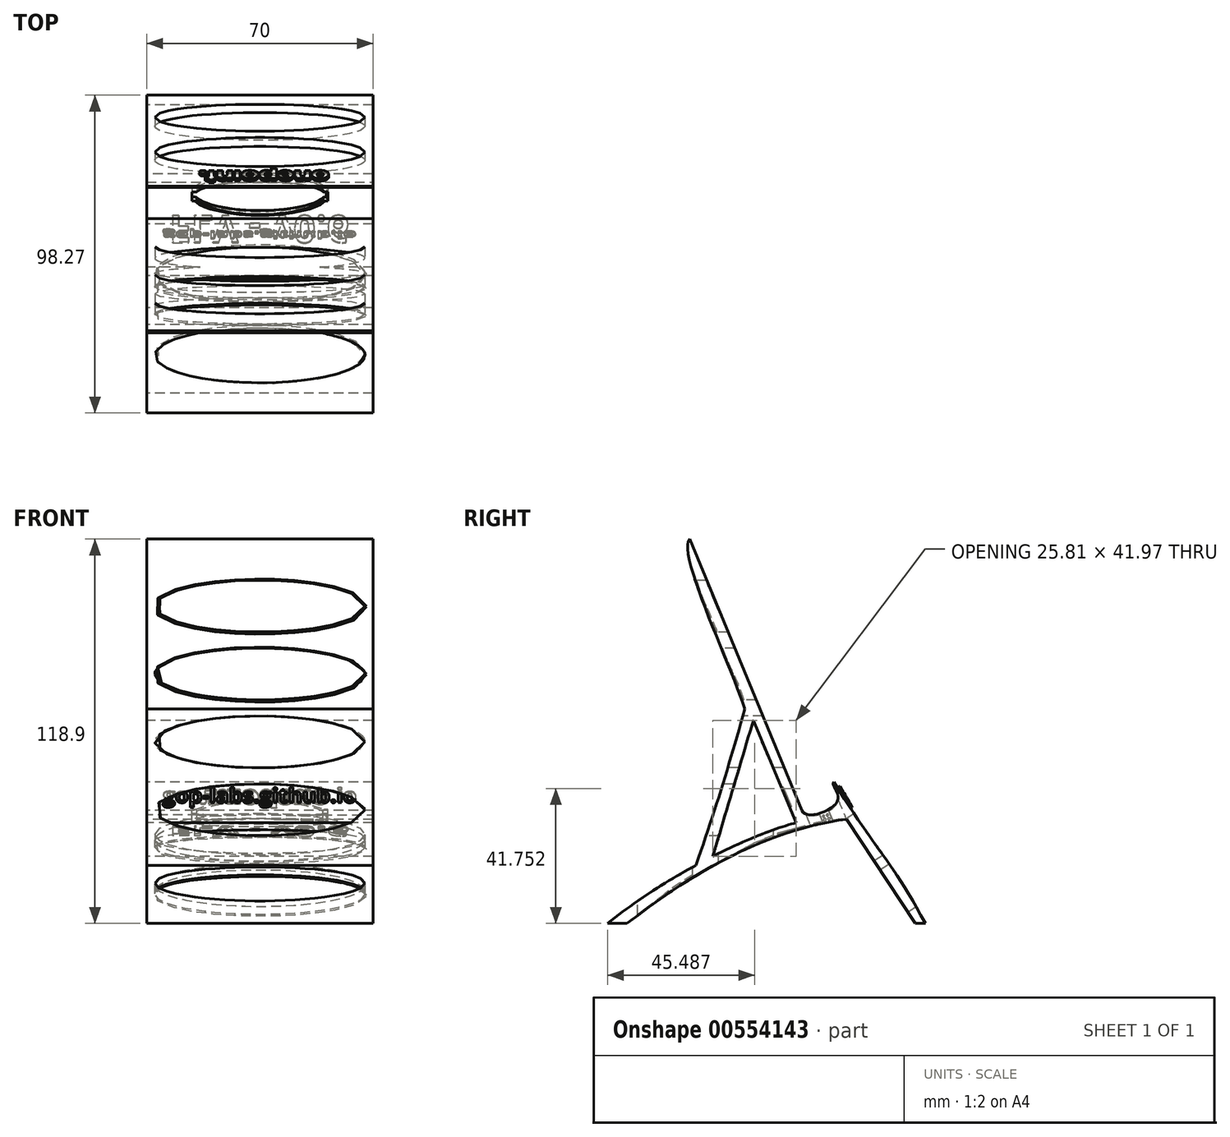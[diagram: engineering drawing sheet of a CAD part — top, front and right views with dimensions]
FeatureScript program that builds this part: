
annotation { "Feature Type Name" : "Feature", "Feature Type Description" : "" }
export const myFeature = defineFeature(function(context is Context, id is Id, definition is map)
    precondition{}
    {
        {
            var Q0;
            Q0=qCreatedBy(makeId("Right.planeOp"),FACE);
            var sketch = newSketch(context, id + "F0", { "sketchPlane" : qUnion([Q0])});
            skFitSpline(sketch, "E0", {"points": [v(42.97, 20.37) * mm, v(14.77, 64.07) * mm], "startDerivative": vector(-33.57, 62.35) * mm, "endDerivative": vector(-38.78, 64) * mm});
            skLineSegment(sketch, "E1", {"start": v(-29.92, 139.27) * mm, "end": v(4.83, 55.39) * mm});
            skFitSpline(sketch, "E2", {"points": [v(4.83, 55.39) * mm, v(15.94, 58.63) * mm, v(14.77, 64.07) * mm], "startDerivative": vector(5.7, -17.02) * mm, "endDerivative": vector(10.42, 3.26) * mm});
            skLineSegment(sketch, "E3", {"start": v(18.6, 52.58) * mm, "end": v(39.9, 20.37) * mm});
            skLineSegment(sketch, "E4", {"start": v(-10.23, 83.1) * mm, "end": v(3.1, 51.52) * mm});
            skFitSpline(sketch, "E5", {"points": [v(-29.92, 139.27) * mm, v(-12.82, 86.66) * mm], "startDerivative": vector(-12.17, -12.55) * mm, "endDerivative": vector(13.11, -40.92) * mm});
            skFitSpline(sketch, "E6", {"points": [v(3.1, 51.52) * mm, v(-55.3, 20.37) * mm], "startDerivative": vector(-34.97, -8.7) * mm, "endDerivative": vector(-63.71, -51.04) * mm});
            skFitSpline(sketch, "E7", {"points": [v(18.6, 52.58) * mm, v(-49.24, 20.37) * mm], "startDerivative": vector(-55.78, -6.95) * mm, "endDerivative": vector(-79.56, -62.3) * mm});
            skLineSegment(sketch, "E8", {"start": v(-49.24, 20.37) * mm, "end": v(-55.3, 20.37) * mm});
            skLineSegment(sketch, "E9", {"start": v(42.97, 20.37) * mm, "end": v(39.9, 20.37) * mm});
            skLineSegment(sketch, "E10", {"start": v(39.9, 20.37) * mm, "end": v(-49.24, 20.37) * mm});
            skFitSpline(sketch, "E11", {"points": [v(-10.23, 83.1) * mm, v(-22.72, 41.14) * mm], "startDerivative": vector(-11.4, -38.7) * mm, "endDerivative": vector(-11.4, -38.7) * mm});
            skFitSpline(sketch, "E12", {"points": [v(-12.82, 86.66) * mm, v(-27.98, 38.37) * mm], "startDerivative": vector(-14.28, -50.37) * mm, "endDerivative": vector(-17.92, -50.53) * mm});
            skSolve(sketch);
        }
        {
            var Q0;
            Q0=makeQuery(id+"F0.imprint","IMPRINT",FACE,{"disambiguationData":[TD([[makeQuery(id+"F0.imprint","IMPRINT",EDGE,{"derivedFrom":sQuery(id+"F0.wireOp",EDGE,"e2dd9e04-bce8-43ee-a2f2-a46b7d135692")}),-1.0]])]});
            var Q1;
            Q1=makeQuery(id+"F0.imprint","IMPRINT",FACE,{"disambiguationData":[TD([[makeQuery(id+"F0.imprint","IMPRINT",EDGE,{"derivedFrom":sQuery(id+"F0.wireOp",EDGE,"dd02e322-1caa-4adf-9807-8f987be65d11")}),1.0]])]});
            var Q2;
            Q2=makeQuery(id+"F0.imprint","IMPRINT",FACE,{"disambiguationData":[TD([[makeQuery(id+"F0.imprint","IMPRINT",EDGE,{"derivedFrom":sQuery(id+"F0.wireOp",EDGE,"E0")}),1.0]])]});
            var Q3;
            {var subQ0=sQuery(id+"F0.wireOp",EDGE,"E6");Q3=makeQuery(id+"F0.imprint","IMPRINT",FACE,{"disambiguationData":[TD([[makeQuery(id+"F0.imprint","IMPRINT",EDGE,{"derivedFrom":subQ0}),1.0]])]});}
            extrude(context, id + "F1", {"entities" : qUnion([Q0, Q1, Q2, Q3]), "depth" : 70 * mm});
        }
        {
            var Q0;
            Q0=makeQuery(id+"F1.opExtrude","SWEPT_FACE",FACE,{"disambiguationData":[OSD([sQuery(id+"F0.wireOp",EDGE,"E3")])]});
            var sketch = newSketch(context, id + "F2", { "sketchPlane" : qUnion([Q0])});
            skEllipse(sketch, "E13", {"center": v(35, 25.97) * mm, "majorRadius": 32.5 * mm, "minorRadius": 7.82 * mm, "majorAxis": v(1, 0)});
            skEllipse(sketch, "E14.0.1.0", {"center": v(35, 6.97) * mm, "majorRadius": 32.5 * mm, "minorRadius": 7.82 * mm, "majorAxis": v(1, 0)});
            skLineSegment(sketch, "E14.direction1", {"start": v(35, 25.97) * mm, "end": v(57.03, 25.97) * mm, "construction": true});
            skLineSegment(sketch, "E14.direction2", {"start": v(35, 25.97) * mm, "end": v(35, 6.97) * mm, "construction": true});
            skSolve(sketch);
        }
        {
            var Q0;
            Q0=qSketchRegion(id+"F2",true);
            var Q1;
            Q1=makeQuery(id+"F1.opExtrude","SWEPT_FACE",FACE,{"disambiguationData":[OSD([sQuery(id+"F0.wireOp",EDGE,"E0")])]});
            extrude(context, id + "F3", {"entities" : qUnion([Q0]), "operationType" : NewBodyOperationType.REMOVE, "endBound" : BoundingType.UP_TO_SURFACE, "oppositeDirection" : true, "endBoundEntityFace" : qUnion([Q1]), "depth" : 25 * mm});
        }
        {
            var Q0;
            Q0=qCreatedBy(makeId("Top.planeOp"),FACE);
            var sketch = newSketch(context, id + "F4", { "sketchPlane" : qUnion([Q0])});
            skEllipse(sketch, "E15", {"center": v(35, -37.48) * mm, "majorRadius": 32.5 * mm, "minorRadius": 8.5 * mm, "majorAxis": v(1, 0)});
            skEllipse(sketch, "E16.0.1.0", {"center": v(35, -12.48) * mm, "majorRadius": 32.5 * mm, "minorRadius": 8.5 * mm, "majorAxis": v(1, 0)});
            skLineSegment(sketch, "E16.direction1", {"start": v(35, -37.48) * mm, "end": v(60, -37.48) * mm, "construction": true});
            skLineSegment(sketch, "E16.direction2", {"start": v(35, -37.48) * mm, "end": v(35, -12.48) * mm, "construction": true});
            skSolve(sketch);
        }
        {
            var Q0;
            Q0=makeQuery(id+"F4.imprint","IMPRINT",FACE,{"disambiguationData":[TD([[makeQuery(id+"F4.imprint","IMPRINT",EDGE,{"derivedFrom":sQuery(id+"F4.wireOp",EDGE,"E16.0.1.0")}),1.0]])]});
            var Q1;
            Q1=makeQuery(id+"F4.imprint","IMPRINT",FACE,{"disambiguationData":[TD([[makeQuery(id+"F4.imprint","IMPRINT",EDGE,{"derivedFrom":sQuery(id+"F4.wireOp",EDGE,"E16.0.2.0")}),1.0]])]});
            var Q2;
            Q2=makeQuery(id+"F1.opExtrude","SWEPT_FACE",FACE,{"disambiguationData":[OSD([sQuery(id+"F0.wireOp",EDGE,"E6")])]});
            extrude(context, id + "F5", {"entities" : qUnion([Q0, Q1]), "operationType" : NewBodyOperationType.REMOVE, "endBound" : BoundingType.UP_TO_SURFACE, "endBoundEntityFace" : qUnion([Q2]), "depth" : 25 * mm});
        }
        {
            var Q0;
            Q0=qCreatedBy(makeId("Front.planeOp"),FACE);
            cPlane(context, id + "F6", {"entities" : qUnion([Q0]), "cplaneType" : CPlaneType.OFFSET, "offset" : 70 * mm, "width" : 150 * mm, "height" : 150 * mm});
        }
        {
            var Q0;
            Q0=qCreatedBy(id+"F6.planeOp",FACE);
            var sketch = newSketch(context, id + "F7", { "sketchPlane" : qUnion([Q0])});
            skEllipse(sketch, "E17", {"center": v(35, 118.52) * mm, "majorRadius": 32.5 * mm, "minorRadius": 8 * mm, "majorAxis": v(1, 0)});
            skEllipse(sketch, "E18.0.1.0", {"center": v(35, 97.52) * mm, "majorRadius": 32.5 * mm, "minorRadius": 8 * mm, "majorAxis": v(1, 0)});
            skEllipse(sketch, "E18.0.2.0", {"center": v(35, 76.52) * mm, "majorRadius": 32.5 * mm, "minorRadius": 8 * mm, "majorAxis": v(1, 0)});
            skEllipse(sketch, "E18.0.3.0", {"center": v(35, 55.52) * mm, "majorRadius": 32.5 * mm, "minorRadius": 8 * mm, "majorAxis": v(1, 0)});
            skEllipse(sketch, "E18.0.4.0", {"center": v(35, 34.52) * mm, "majorRadius": 32.5 * mm, "minorRadius": 8 * mm, "majorAxis": v(1, 0)});
            skEllipse(sketch, "E18.0.5.0", {"center": v(35, 13.52) * mm, "majorRadius": 32.5 * mm, "minorRadius": 8 * mm, "majorAxis": v(1, 0)});
            skLineSegment(sketch, "E18.direction1", {"start": v(35, 118.52) * mm, "end": v(60, 118.52) * mm, "construction": true});
            skLineSegment(sketch, "E18.direction2", {"start": v(35, 118.52) * mm, "end": v(35, 97.52) * mm, "construction": true});
            skSolve(sketch);
        }
        {
            var Q0;
            Q0=makeQuery(id+"F7.imprint","IMPRINT",FACE,{"disambiguationData":[TD([[makeQuery(id+"F7.imprint","IMPRINT",EDGE,{"derivedFrom":sQuery(id+"F7.wireOp",EDGE,"E18.0.3.0")}),1.0]])]});
            var Q1;
            Q1=makeQuery(id+"F1.opExtrude","SWEPT_FACE",FACE,{"disambiguationData":[OSD([sQuery(id+"F0.wireOp",EDGE,"E11")])]});
            extrude(context, id + "F8", {"entities" : qUnion([Q0]), "operationType" : NewBodyOperationType.REMOVE, "endBound" : BoundingType.UP_TO_SURFACE, "oppositeDirection" : true, "endBoundEntityFace" : qUnion([Q1]), "depth" : 25 * mm});
        }
        {
            var Q0;
            Q0=makeQuery(id+"F7.imprint","IMPRINT",FACE,{"disambiguationData":[TD([[makeQuery(id+"F7.imprint","IMPRINT",EDGE,{"derivedFrom":sQuery(id+"F7.wireOp",EDGE,"E17")}),1.0]])]});
            var Q1;
            Q1=makeQuery(id+"F7.imprint","IMPRINT",FACE,{"disambiguationData":[TD([[makeQuery(id+"F7.imprint","IMPRINT",EDGE,{"derivedFrom":sQuery(id+"F7.wireOp",EDGE,"E18.0.1.0")}),1.0]])]});
            var Q2;
            Q2=makeQuery(id+"F7.imprint","IMPRINT",FACE,{"disambiguationData":[TD([[makeQuery(id+"F7.imprint","IMPRINT",EDGE,{"derivedFrom":sQuery(id+"F7.wireOp",EDGE,"E18.0.2.0")}),1.0]])]});
            var Q3;
            Q3=makeQuery(id+"F1.opExtrude","SWEPT_FACE",FACE,{"disambiguationData":[OSD([sQuery(id+"F0.wireOp",EDGE,"E1")])]});
            extrude(context, id + "F9", {"entities" : qUnion([Q0, Q1, Q2]), "operationType" : NewBodyOperationType.REMOVE, "endBound" : BoundingType.UP_TO_SURFACE, "oppositeDirection" : true, "endBoundEntityFace" : qUnion([Q3]), "depth" : 25 * mm});
        }
        {
            var Q0;
            Q0=makeQuery(id+"F1.opExtrude","SWEPT_FACE",FACE,{"disambiguationData":[OSD([sQuery(id+"F0.wireOp",EDGE,"E1")])]});
            var Q1;
            Q1=makeQuery(id+"F1.opExtrude","SWEPT_EDGE",EDGE,{"disambiguationData":[OSD([sQuery(id+"F0.wireOp",EDGE,"E1"),sQuery(id+"F0.wireOp",EDGE,"E5")])]});
            cPlane(context, id + "F10", {"entities" : qUnion([Q0, Q1]), "cplaneType" : CPlaneType.LINE_ANGLE, "offset" : 25 * mm, "angle" : 90 * degree, "width" : 150 * mm, "height" : 150 * mm});
        }
        {
            var Q0;
            Q0=qCreatedBy(id+"F10.planeOp",FACE);
            var sketch = newSketch(context, id + "F11", { "sketchPlane" : qUnion([Q0])});
            skEllipse(sketch, "E19", {"center": v(35, 31.76) * mm, "majorRadius": 20.25 * mm, "minorRadius": 5.5 * mm, "majorAxis": v(-1, 0)});
            skLineSegment(sketch, "E20.bottom", {"start": v(14, 30.26) * mm, "end": v(56, 30.26) * mm});
            skLineSegment(sketch, "E20.top", {"start": v(14, 33.26) * mm, "end": v(56, 33.26) * mm});
            skLineSegment(sketch, "E20.left", {"start": v(14, 30.26) * mm, "end": v(14, 33.26) * mm});
            skLineSegment(sketch, "E20.right", {"start": v(56, 30.26) * mm, "end": v(56, 33.26) * mm});
            skSolve(sketch);
        }
        {
            var Q0;
            Q0=qSketchRegion(id+"F11",true);
            var Q1;
            Q1=makeQuery(id+"F1.opExtrude","SWEPT_FACE",FACE,{"disambiguationData":[OSD([sQuery(id+"F0.wireOp",EDGE,"E7")])]});
            extrude(context, id + "F12", {"entities" : qUnion([Q0]), "operationType" : NewBodyOperationType.REMOVE, "endBound" : BoundingType.THROUGH_ALL, "oppositeDirection" : true, "endBoundEntityFace" : qUnion([Q1]), "depth" : 25 * mm});
        }
        {
            var Q0;
            Q0=makeQuery(id+"F3.boolean.opBoolean","COPY",EDGE,{"derivedFrom":makeQuery(id+"F3.opExtrude","TWEAK_EDGE",EDGE,{"derivedFrom":[makeQuery(id+"F1.opExtrude","SWEPT_FACE",FACE,{"disambiguationData":[OSD([sQuery(id+"F0.wireOp",EDGE,"E0")])]}),makeQuery(id+"F2.imprint","IMPRINT",EDGE,{"derivedFrom":sQuery(id+"F2.wireOp",EDGE,"E13")})]})});
            var Q1;
            Q1=makeQuery(id+"F3.boolean.opBoolean","COPY",EDGE,{"derivedFrom":makeQuery(id+"F3.opExtrude","TWEAK_EDGE",EDGE,{"derivedFrom":[makeQuery(id+"F1.opExtrude","SWEPT_FACE",FACE,{"disambiguationData":[OSD([sQuery(id+"F0.wireOp",EDGE,"E0")])]}),makeQuery(id+"F2.imprint","IMPRINT",EDGE,{"derivedFrom":sQuery(id+"F2.wireOp",EDGE,"E14.0.1.0")})]})});
            var Q2;
            Q2=makeQuery(id+"F3.boolean.opBoolean","COPY",EDGE,{"derivedFrom":makeQuery(id+"F3.opExtrude","TWEAK_EDGE",EDGE,{"derivedFrom":[makeQuery(id+"F1.opExtrude","SWEPT_FACE",FACE,{"disambiguationData":[OSD([sQuery(id+"F0.wireOp",EDGE,"E0")])]}),makeQuery(id+"F2.imprint","IMPRINT",EDGE,{"derivedFrom":sQuery(id+"F2.wireOp",EDGE,"E14.0.2.0")})]})});
            var Q3;
            Q3=makeQuery(id+"F3.boolean.opBoolean","COPY",EDGE,{"derivedFrom":makeQuery(id+"F3.opExtrude","CAP_EDGE",EDGE,{"disambiguationData":[OSD([sQuery(id+"F2.wireOp",EDGE,"E13")])],"isStart":true})});
            var Q4;
            Q4=makeQuery(id+"F3.boolean.opBoolean","COPY",EDGE,{"derivedFrom":makeQuery(id+"F3.opExtrude","CAP_EDGE",EDGE,{"disambiguationData":[OSD([sQuery(id+"F2.wireOp",EDGE,"E14.0.1.0")])],"isStart":true})});
            var Q5;
            Q5=makeQuery(id+"F3.boolean.opBoolean","COPY",EDGE,{"derivedFrom":makeQuery(id+"F3.opExtrude","CAP_EDGE",EDGE,{"disambiguationData":[OSD([sQuery(id+"F2.wireOp",EDGE,"E14.0.2.0")])],"isStart":true})});
            var Q6;
            Q6=makeQuery(id+"F8.boolean.opBoolean","INTERSECT",EDGE,{"derivedFrom":[makeQuery(id+"F1.opExtrude","SWEPT_FACE",FACE,{"disambiguationData":[OSD([sQuery(id+"F0.wireOp",EDGE,"61fd75d5-24df-4c68-a095-90f6d82b9ead")])]}),makeQuery(id+"F8.opExtrude","SWEPT_FACE",FACE,{"disambiguationData":[OSD([sQuery(id+"F7.wireOp",EDGE,"E18.0.3.0")])]})]});
            var Q7;
            Q7=makeQuery(id+"F8.boolean.opBoolean","COPY",EDGE,{"derivedFrom":makeQuery(id+"F8.opExtrude","CAP_EDGE",EDGE,{"disambiguationData":[OSD([sQuery(id+"F7.wireOp",EDGE,"E18.0.3.0")])],"isStart":false})});
            var Q8;
            Q8=makeQuery(id+"F8.boolean.opBoolean","INTERSECT",EDGE,{"derivedFrom":[makeQuery(id+"F1.opExtrude","SWEPT_FACE",FACE,{"disambiguationData":[OSD([sQuery(id+"F0.wireOp",EDGE,"61fd75d5-24df-4c68-a095-90f6d82b9ead")])]}),makeQuery(id+"F8.opExtrude","SWEPT_FACE",FACE,{"disambiguationData":[OSD([sQuery(id+"F7.wireOp",EDGE,"E18.0.4.0")])]})]});
            var Q9;
            {var subQ0=sQuery(id+"F0.wireOp",EDGE,"5998eb2a-c125-4484-9ba4-89ed062cae3a");var subQ1=sQuery(id+"F0.wireOp",EDGE,"E7");var subQ2=sQuery(id+"F7.wireOp",EDGE,"E18.0.4.0");Q9=makeQuery(id+"F8.boolean.opBoolean","COPY",EDGE,{"disambiguationData":[TD([makeQuery(id+"F1.opExtrude","SWEPT_FACE",FACE,{"disambiguationData":[OSD([subQ0]),TDD([makeQuery(id+"F0.imprint","IMPRINT",EDGE,{"disambiguationData":[TD([[makeQuery(id+"F0.imprint","INTERSECT",VERTEX,{"derivedFrom":[subQ0,sQuery(id+"F0.wireOp",EDGE,"umK4nLRB-749r-FOEl-6r3i-m92kNIwFStfI")]}),-1.0]])],"derivedFrom":subQ0})])]}),makeQuery(id+"F1.opExtrude","SWEPT_FACE",FACE,{"disambiguationData":[OSD([subQ1])]}),makeQuery(id+"F8.opExtrude","SWEPT_FACE",FACE,{"disambiguationData":[OSD([subQ2])]}),makeQuery(id+"F8.opExtrude","CAP_FACE",FACE,{"disambiguationData":[OSD([subQ2])],"isStart":false})])],"derivedFrom":makeQuery(id+"F8.opExtrude","CAP_EDGE",EDGE,{"disambiguationData":[OSD([subQ2])],"isStart":false})});}
            var Q10;
            Q10=makeQuery(id+"F8.boolean.opBoolean","INTERSECT",EDGE,{"derivedFrom":[makeQuery(id+"F1.opExtrude","SWEPT_FACE",FACE,{"disambiguationData":[OSD([sQuery(id+"F0.wireOp",EDGE,"61fd75d5-24df-4c68-a095-90f6d82b9ead")])]}),makeQuery(id+"F8.opExtrude","SWEPT_FACE",FACE,{"disambiguationData":[OSD([sQuery(id+"F7.wireOp",EDGE,"E18.0.5.0")])]})]});
            var Q11;
            Q11=makeQuery(id+"F8.boolean.opBoolean","COPY",EDGE,{"derivedFrom":makeQuery(id+"F8.opExtrude","CAP_EDGE",EDGE,{"disambiguationData":[OSD([sQuery(id+"F7.wireOp",EDGE,"E18.0.5.0")])],"isStart":false})});
            var Q12;
            {var subQ0=sQuery(id+"F0.wireOp",EDGE,"5998eb2a-c125-4484-9ba4-89ed062cae3a");Q12=makeQuery(id+"F9.boolean.opBoolean","INTERSECT",EDGE,{"derivedFrom":[makeQuery(id+"F1.opExtrude","SWEPT_FACE",FACE,{"disambiguationData":[OSD([subQ0]),TDD([makeQuery(id+"F0.imprint","IMPRINT",EDGE,{"disambiguationData":[TD([[makeQuery(id+"F0.imprint","INTERSECT",VERTEX,{"derivedFrom":[subQ0,sQuery(id+"F0.wireOp",EDGE,"E4")]}),1.0]])],"derivedFrom":subQ0})])]}),makeQuery(id+"F9.opExtrude","SWEPT_FACE",FACE,{"disambiguationData":[OSD([sQuery(id+"F7.wireOp",EDGE,"E18.0.2.0")])]})]});}
            var Q13;
            Q13=makeQuery(id+"F9.boolean.opBoolean","INTERSECT",EDGE,{"derivedFrom":[makeQuery(id+"F1.opExtrude","SWEPT_FACE",FACE,{"disambiguationData":[OSD([sQuery(id+"F0.wireOp",EDGE,"61fd75d5-24df-4c68-a095-90f6d82b9ead")])]}),makeQuery(id+"F9.opExtrude","SWEPT_FACE",FACE,{"disambiguationData":[OSD([sQuery(id+"F7.wireOp",EDGE,"E18.0.2.0")])]})]});
            var Q14;
            Q14=makeQuery(id+"F5.boolean.opBoolean","COPY",EDGE,{"derivedFrom":makeQuery(id+"F5.opExtrude","TWEAK_EDGE",EDGE,{"derivedFrom":[makeQuery(id+"F1.opExtrude","SWEPT_FACE",FACE,{"disambiguationData":[OSD([sQuery(id+"F0.wireOp",EDGE,"E6")])]}),makeQuery(id+"F4.imprint","IMPRINT",EDGE,{"derivedFrom":sQuery(id+"F4.wireOp",EDGE,"E16.0.1.0")})]})});
            var Q15;
            Q15=makeQuery(id+"F5.boolean.opBoolean","INTERSECT",EDGE,{"derivedFrom":[makeQuery(id+"F1.opExtrude","SWEPT_FACE",FACE,{"disambiguationData":[OSD([sQuery(id+"F0.wireOp",EDGE,"E7")])]}),makeQuery(id+"F5.opExtrude","SWEPT_FACE",FACE,{"disambiguationData":[OSD([sQuery(id+"F4.wireOp",EDGE,"E16.0.1.0")])]})]});
            var Q16;
            Q16=makeQuery(id+"F5.boolean.opBoolean","INTERSECT",EDGE,{"derivedFrom":[makeQuery(id+"F1.opExtrude","SWEPT_FACE",FACE,{"disambiguationData":[OSD([sQuery(id+"F0.wireOp",EDGE,"E7")])]}),makeQuery(id+"F5.opExtrude","SWEPT_FACE",FACE,{"disambiguationData":[OSD([sQuery(id+"F4.wireOp",EDGE,"E15")])]})]});
            var Q17;
            Q17=makeQuery(id+"F5.boolean.opBoolean","COPY",EDGE,{"derivedFrom":makeQuery(id+"F5.opExtrude","TWEAK_EDGE",EDGE,{"derivedFrom":[makeQuery(id+"F1.opExtrude","SWEPT_FACE",FACE,{"disambiguationData":[OSD([sQuery(id+"F0.wireOp",EDGE,"E6")])]}),makeQuery(id+"F4.imprint","IMPRINT",EDGE,{"derivedFrom":sQuery(id+"F4.wireOp",EDGE,"E15")})]})});
            var Q18;
            Q18=makeQuery(id+"F9.boolean.opBoolean","COPY",EDGE,{"derivedFrom":makeQuery(id+"F9.opExtrude","TWEAK_EDGE",EDGE,{"derivedFrom":[makeQuery(id+"F1.opExtrude","SWEPT_FACE",FACE,{"disambiguationData":[OSD([sQuery(id+"F0.wireOp",EDGE,"E1")])]}),makeQuery(id+"F7.imprint","IMPRINT",EDGE,{"derivedFrom":sQuery(id+"F7.wireOp",EDGE,"E18.0.2.0")})]})});
            var Q19;
            Q19=makeQuery(id+"F9.boolean.opBoolean","COPY",EDGE,{"derivedFrom":makeQuery(id+"F9.opExtrude","TWEAK_EDGE",EDGE,{"derivedFrom":[makeQuery(id+"F1.opExtrude","SWEPT_FACE",FACE,{"disambiguationData":[OSD([sQuery(id+"F0.wireOp",EDGE,"E1")])]}),makeQuery(id+"F7.imprint","IMPRINT",EDGE,{"derivedFrom":sQuery(id+"F7.wireOp",EDGE,"E18.0.1.0")})]})});
            var Q20;
            Q20=makeQuery(id+"F9.boolean.opBoolean","INTERSECT",EDGE,{"derivedFrom":[makeQuery(id+"F1.opExtrude","SWEPT_FACE",FACE,{"disambiguationData":[OSD([sQuery(id+"F0.wireOp",EDGE,"E5")])]}),makeQuery(id+"F9.opExtrude","SWEPT_FACE",FACE,{"disambiguationData":[OSD([sQuery(id+"F7.wireOp",EDGE,"E18.0.1.0")])]})]});
            var Q21;
            Q21=makeQuery(id+"F9.boolean.opBoolean","INTERSECT",EDGE,{"derivedFrom":[makeQuery(id+"F1.opExtrude","SWEPT_FACE",FACE,{"disambiguationData":[OSD([sQuery(id+"F0.wireOp",EDGE,"E5")])]}),makeQuery(id+"F9.opExtrude","SWEPT_FACE",FACE,{"disambiguationData":[OSD([sQuery(id+"F7.wireOp",EDGE,"E17")])]})]});
            var Q22;
            Q22=makeQuery(id+"F9.boolean.opBoolean","COPY",EDGE,{"derivedFrom":makeQuery(id+"F9.opExtrude","TWEAK_EDGE",EDGE,{"derivedFrom":[makeQuery(id+"F1.opExtrude","SWEPT_FACE",FACE,{"disambiguationData":[OSD([sQuery(id+"F0.wireOp",EDGE,"E1")])]}),makeQuery(id+"F7.imprint","IMPRINT",EDGE,{"derivedFrom":sQuery(id+"F7.wireOp",EDGE,"E17")})]})});
            fillet(context, id + "F13", {"entities" : qUnion([Q0, Q1, Q2, Q3, Q4, Q5, Q6, Q7, Q8, Q9, Q10, Q11, Q12, Q13, Q14, Q15, Q16, Q17, Q18, Q19, Q20, Q21, Q22]), "radius" : 0.5 * mm, "tangentPropagation" : true, "allowEdgeOverflow" : false});
        }
        {
            var Q0;
            Q0=makeQuery(id+"F1.opExtrude","SWEPT_EDGE",EDGE,{"disambiguationData":[OSD([sQuery(id+"F0.wireOp",EDGE,"E0"),sQuery(id+"F0.wireOp",EDGE,"E2")])]});
            cPlane(context, id + "F14", {"entities" : qUnion([Q0]), "cplaneType" : CPlaneType.LINE_ANGLE, "offset" : 25 * mm, "angle" : 150 * degree, "width" : 150 * mm, "height" : 150 * mm});
        }
        {
            var Q0;
            Q0=qCreatedBy(id+"F14.planeOp",FACE);
            var sketch = newSketch(context, id + "F15", { "sketchPlane" : qUnion([Q0])});
            skLineSegment(sketch, "E21", {"start": v(-54.12, 39.93) * mm, "end": v(-54.9, 40.17) * mm});
            skLineSegment(sketch, "E22", {"start": v(-54.9, 40.17) * mm, "end": v(-55.54, 40.6) * mm});
            skLineSegment(sketch, "E23", {"start": v(-55.54, 40.6) * mm, "end": v(-56.02, 41.2) * mm});
            skLineSegment(sketch, "E24", {"start": v(-56.02, 41.2) * mm, "end": v(-56.3, 41.94) * mm});
            skLineSegment(sketch, "E25", {"start": v(-56.3, 41.94) * mm, "end": v(-56.33, 42.13) * mm});
            skLineSegment(sketch, "E26", {"start": v(-56.33, 42.13) * mm, "end": v(-56.34, 42.37) * mm});
            skLineSegment(sketch, "E27", {"start": v(-56.34, 42.62) * mm, "end": v(-56.32, 42.83) * mm});
            skLineSegment(sketch, "E28", {"start": v(-56.32, 42.83) * mm, "end": v(-56.06, 43.6) * mm});
            skLineSegment(sketch, "E29", {"start": v(-56.06, 43.6) * mm, "end": v(-55.56, 44.26) * mm});
            skLineSegment(sketch, "E30", {"start": v(-55.56, 44.26) * mm, "end": v(-55.18, 44.57) * mm});
            skLineSegment(sketch, "E31", {"start": v(-55.18, 44.57) * mm, "end": v(-54.75, 44.8) * mm});
            skLineSegment(sketch, "E32", {"start": v(-54.75, 44.8) * mm, "end": v(-54.28, 44.94) * mm});
            skLineSegment(sketch, "E33", {"start": v(-54.28, 44.94) * mm, "end": v(-53.77, 45) * mm});
            skLineSegment(sketch, "E34", {"start": v(-53.77, 45) * mm, "end": v(-53.19, 44.98) * mm});
            skLineSegment(sketch, "E35", {"start": v(-53.19, 44.98) * mm, "end": v(-52.64, 44.84) * mm});
            skLineSegment(sketch, "E36", {"start": v(-52.64, 44.84) * mm, "end": v(-52.15, 44.6) * mm});
            skLineSegment(sketch, "E37", {"start": v(-52.15, 44.6) * mm, "end": v(-51.7, 44.26) * mm});
            skLineSegment(sketch, "E38", {"start": v(-51.7, 44.26) * mm, "end": v(-51.23, 43.63) * mm});
            skLineSegment(sketch, "E39", {"start": v(-51.23, 43.63) * mm, "end": v(-50.98, 42.9) * mm});
            skLineSegment(sketch, "E40", {"start": v(-50.98, 42.9) * mm, "end": v(-50.95, 42.7) * mm});
            skLineSegment(sketch, "E41", {"start": v(-50.95, 42.7) * mm, "end": v(-50.95, 42.45) * mm});
            skLineSegment(sketch, "E42", {"start": v(-50.95, 42.45) * mm, "end": v(-50.96, 42.2) * mm});
            skLineSegment(sketch, "E43", {"start": v(-50.96, 42.2) * mm, "end": v(-50.99, 42) * mm});
            skLineSegment(sketch, "E44", {"start": v(-50.99, 42) * mm, "end": v(-51.26, 41.25) * mm});
            skLineSegment(sketch, "E45", {"start": v(-51.26, 41.25) * mm, "end": v(-51.73, 40.64) * mm});
            skLineSegment(sketch, "E46", {"start": v(-51.73, 40.64) * mm, "end": v(-52.37, 40.19) * mm});
            skLineSegment(sketch, "E47", {"start": v(-52.37, 40.19) * mm, "end": v(-53.14, 39.94) * mm});
            skLineSegment(sketch, "E48", {"start": v(-53.14, 39.94) * mm, "end": v(-53.63, 39.9) * mm});
            skLineSegment(sketch, "E49", {"start": v(-53.63, 39.9) * mm, "end": v(-54.12, 39.93) * mm});
            skLineSegment(sketch, "E50", {"start": v(-54.12, 39.93) * mm, "end": v(-54.12, 39.93) * mm});
            skLineSegment(sketch, "E51", {"start": v(-53.38, 41.4) * mm, "end": v(-53.15, 41.5) * mm});
            skLineSegment(sketch, "E52", {"start": v(-53.15, 41.5) * mm, "end": v(-52.96, 41.63) * mm});
            skLineSegment(sketch, "E53", {"start": v(-52.96, 41.63) * mm, "end": v(-52.8, 41.82) * mm});
            skLineSegment(sketch, "E54", {"start": v(-52.8, 41.82) * mm, "end": v(-52.7, 42.06) * mm});
            skLineSegment(sketch, "E55", {"start": v(-52.7, 42.06) * mm, "end": v(-52.63, 42.42) * mm});
            skLineSegment(sketch, "E56", {"start": v(-52.63, 42.42) * mm, "end": v(-52.67, 42.77) * mm});
            skLineSegment(sketch, "E57", {"start": v(-52.67, 42.77) * mm, "end": v(-52.8, 43.04) * mm});
            skLineSegment(sketch, "E58", {"start": v(-52.8, 43.04) * mm, "end": v(-52.97, 43.26) * mm});
            skLineSegment(sketch, "E59", {"start": v(-52.97, 43.26) * mm, "end": v(-53.2, 43.42) * mm});
            skLineSegment(sketch, "E60", {"start": v(-53.2, 43.42) * mm, "end": v(-53.46, 43.52) * mm});
            skLineSegment(sketch, "E61", {"start": v(-53.46, 43.52) * mm, "end": v(-53.57, 43.54) * mm});
            skLineSegment(sketch, "E62", {"start": v(-53.57, 43.54) * mm, "end": v(-53.66, 43.55) * mm});
            skLineSegment(sketch, "E63", {"start": v(-53.66, 43.55) * mm, "end": v(-53.88, 43.52) * mm});
            skLineSegment(sketch, "E64", {"start": v(-53.88, 43.52) * mm, "end": v(-54.1, 43.44) * mm});
            skLineSegment(sketch, "E65", {"start": v(-54.1, 43.44) * mm, "end": v(-54.28, 43.32) * mm});
            skLineSegment(sketch, "E66", {"start": v(-54.28, 43.32) * mm, "end": v(-54.43, 43.16) * mm});
            skLineSegment(sketch, "E67", {"start": v(-54.43, 43.16) * mm, "end": v(-54.55, 42.97) * mm});
            skLineSegment(sketch, "E68", {"start": v(-54.55, 42.97) * mm, "end": v(-54.62, 42.76) * mm});
            skLineSegment(sketch, "E69", {"start": v(-54.62, 42.76) * mm, "end": v(-54.65, 42.62) * mm});
            skLineSegment(sketch, "E70", {"start": v(-54.65, 42.62) * mm, "end": v(-54.66, 42.46) * mm});
            skLineSegment(sketch, "E71", {"start": v(-54.66, 42.46) * mm, "end": v(-54.65, 42.3) * mm});
            skLineSegment(sketch, "E72", {"start": v(-54.65, 42.3) * mm, "end": v(-54.62, 42.18) * mm});
            skLineSegment(sketch, "E73", {"start": v(-54.62, 42.18) * mm, "end": v(-54.52, 41.9) * mm});
            skLineSegment(sketch, "E74", {"start": v(-54.52, 41.9) * mm, "end": v(-54.35, 41.68) * mm});
            skLineSegment(sketch, "E75", {"start": v(-54.35, 41.68) * mm, "end": v(-54.14, 41.5) * mm});
            skLineSegment(sketch, "E76", {"start": v(-54.14, 41.5) * mm, "end": v(-53.89, 41.4) * mm});
            skLineSegment(sketch, "E77", {"start": v(-53.89, 41.4) * mm, "end": v(-53.64, 41.37) * mm});
            skLineSegment(sketch, "E78", {"start": v(-53.64, 41.37) * mm, "end": v(-53.38, 41.4) * mm});
            skLineSegment(sketch, "E79", {"start": v(-53.38, 41.4) * mm, "end": v(-53.38, 41.4) * mm});
            skLineSegment(sketch, "E80", {"start": v(-50.6, 42.43) * mm, "end": v(-50.6, 44.87) * mm});
            skLineSegment(sketch, "E81", {"start": v(-50.6, 44.87) * mm, "end": v(-48.87, 44.87) * mm});
            skLineSegment(sketch, "E82", {"start": v(-48.87, 44.87) * mm, "end": v(-48.87, 44.24) * mm});
            skLineSegment(sketch, "E83", {"start": v(-48.87, 44.24) * mm, "end": v(-48.68, 44.42) * mm});
            skLineSegment(sketch, "E84", {"start": v(-48.68, 44.42) * mm, "end": v(-48.43, 44.66) * mm});
            skLineSegment(sketch, "E85", {"start": v(-48.43, 44.66) * mm, "end": v(-48.16, 44.81) * mm});
            skLineSegment(sketch, "E86", {"start": v(-48.16, 44.81) * mm, "end": v(-47.8, 44.94) * mm});
            skLineSegment(sketch, "E87", {"start": v(-47.8, 44.94) * mm, "end": v(-47.4, 44.99) * mm});
            skLineSegment(sketch, "E88", {"start": v(-47.4, 44.99) * mm, "end": v(-47.01, 44.95) * mm});
            skLineSegment(sketch, "E89", {"start": v(-47.01, 44.95) * mm, "end": v(-46.64, 44.83) * mm});
            skLineSegment(sketch, "E90", {"start": v(-46.64, 44.83) * mm, "end": v(-46.33, 44.63) * mm});
            skLineSegment(sketch, "E91", {"start": v(-46.33, 44.63) * mm, "end": v(-46.1, 44.38) * mm});
            skLineSegment(sketch, "E92", {"start": v(-46.1, 44.38) * mm, "end": v(-45.92, 44.06) * mm});
            skLineSegment(sketch, "E93", {"start": v(-45.92, 44.06) * mm, "end": v(-45.8, 43.66) * mm});
            skLineSegment(sketch, "E94", {"start": v(-45.8, 43.66) * mm, "end": v(-45.78, 43.6) * mm});
            skLineSegment(sketch, "E95", {"start": v(-45.78, 43.6) * mm, "end": v(-45.77, 43.52) * mm});
            skLineSegment(sketch, "E96", {"start": v(-45.77, 43.52) * mm, "end": v(-45.77, 43.4) * mm});
            skLineSegment(sketch, "E97", {"start": v(-45.77, 43.4) * mm, "end": v(-45.76, 43.24) * mm});
            skLineSegment(sketch, "E98", {"start": v(-45.76, 43.24) * mm, "end": v(-45.76, 43) * mm});
            skLineSegment(sketch, "E99", {"start": v(-45.76, 43) * mm, "end": v(-45.76, 42.69) * mm});
            skLineSegment(sketch, "E100", {"start": v(-45.76, 42.69) * mm, "end": v(-45.75, 42.27) * mm});
            skLineSegment(sketch, "E101", {"start": v(-45.75, 42.27) * mm, "end": v(-45.75, 41.75) * mm});
            skLineSegment(sketch, "E102", {"start": v(-45.75, 41.75) * mm, "end": v(-45.75, 39.99) * mm});
            skLineSegment(sketch, "E103", {"start": v(-45.75, 39.99) * mm, "end": v(-47.48, 39.99) * mm});
            skLineSegment(sketch, "E104", {"start": v(-47.48, 39.99) * mm, "end": v(-47.48, 41.4) * mm});
            skLineSegment(sketch, "E105", {"start": v(-47.48, 41.4) * mm, "end": v(-47.48, 41.88) * mm});
            skLineSegment(sketch, "E106", {"start": v(-47.48, 41.88) * mm, "end": v(-47.49, 42.23) * mm});
            skLineSegment(sketch, "E107", {"start": v(-47.49, 42.23) * mm, "end": v(-47.5, 42.49) * mm});
            skLineSegment(sketch, "E108", {"start": v(-47.5, 42.49) * mm, "end": v(-47.5, 42.67) * mm});
            skLineSegment(sketch, "E109", {"start": v(-47.5, 42.67) * mm, "end": v(-47.5, 42.79) * mm});
            skLineSegment(sketch, "E110", {"start": v(-47.5, 42.79) * mm, "end": v(-47.5, 42.87) * mm});
            skLineSegment(sketch, "E111", {"start": v(-47.5, 42.87) * mm, "end": v(-47.52, 42.92) * mm});
            skLineSegment(sketch, "E112", {"start": v(-47.52, 42.92) * mm, "end": v(-47.53, 42.96) * mm});
            skLineSegment(sketch, "E113", {"start": v(-47.53, 42.96) * mm, "end": v(-47.62, 43.15) * mm});
            skLineSegment(sketch, "E114", {"start": v(-47.62, 43.15) * mm, "end": v(-47.74, 43.3) * mm});
            skLineSegment(sketch, "E115", {"start": v(-47.74, 43.3) * mm, "end": v(-47.9, 43.4) * mm});
            skLineSegment(sketch, "E116", {"start": v(-47.9, 43.4) * mm, "end": v(-48.1, 43.44) * mm});
            skLineSegment(sketch, "E117", {"start": v(-48.1, 43.44) * mm, "end": v(-48.33, 43.42) * mm});
            skLineSegment(sketch, "E118", {"start": v(-48.33, 43.42) * mm, "end": v(-48.53, 43.34) * mm});
            skLineSegment(sketch, "E119", {"start": v(-48.53, 43.34) * mm, "end": v(-48.7, 43.19) * mm});
            skLineSegment(sketch, "E120", {"start": v(-48.7, 43.19) * mm, "end": v(-48.82, 42.98) * mm});
            skLineSegment(sketch, "E121", {"start": v(-48.82, 42.98) * mm, "end": v(-48.83, 42.94) * mm});
            skLineSegment(sketch, "E122", {"start": v(-48.83, 42.94) * mm, "end": v(-48.84, 42.9) * mm});
            skLineSegment(sketch, "E123", {"start": v(-48.84, 42.9) * mm, "end": v(-48.85, 42.82) * mm});
            skLineSegment(sketch, "E124", {"start": v(-48.85, 42.82) * mm, "end": v(-48.85, 42.7) * mm});
            skLineSegment(sketch, "E125", {"start": v(-48.85, 42.7) * mm, "end": v(-48.86, 42.52) * mm});
            skLineSegment(sketch, "E126", {"start": v(-48.86, 42.52) * mm, "end": v(-48.86, 42.26) * mm});
            skLineSegment(sketch, "E127", {"start": v(-48.86, 42.26) * mm, "end": v(-48.86, 41.9) * mm});
            skLineSegment(sketch, "E128", {"start": v(-48.86, 41.9) * mm, "end": v(-48.87, 41.43) * mm});
            skLineSegment(sketch, "E129", {"start": v(-48.87, 41.43) * mm, "end": v(-48.87, 39.99) * mm});
            skLineSegment(sketch, "E130", {"start": v(-48.87, 39.99) * mm, "end": v(-50.6, 39.99) * mm});
            skLineSegment(sketch, "E131", {"start": v(-50.6, 39.99) * mm, "end": v(-50.6, 42.43) * mm});
            skLineSegment(sketch, "E132", {"start": v(-50.6, 42.43) * mm, "end": v(-50.6, 42.43) * mm});
            skLineSegment(sketch, "E133", {"start": v(-43.28, 39.9) * mm, "end": v(-44.1, 40.15) * mm});
            skLineSegment(sketch, "E134", {"start": v(-44.1, 40.15) * mm, "end": v(-44.75, 40.62) * mm});
            skLineSegment(sketch, "E135", {"start": v(-44.75, 40.62) * mm, "end": v(-45.17, 41.17) * mm});
            skLineSegment(sketch, "E136", {"start": v(-45.17, 41.17) * mm, "end": v(-45.4, 41.84) * mm});
            skLineSegment(sketch, "E137", {"start": v(-45.4, 41.84) * mm, "end": v(-45.43, 41.96) * mm});
            skLineSegment(sketch, "E138", {"start": v(-45.43, 41.96) * mm, "end": v(-45.44, 42.07) * mm});
            skLineSegment(sketch, "E139", {"start": v(-45.44, 42.07) * mm, "end": v(-45.45, 42.22) * mm});
            skLineSegment(sketch, "E140", {"start": v(-45.45, 42.22) * mm, "end": v(-45.45, 42.42) * mm});
            skLineSegment(sketch, "E141", {"start": v(-45.45, 42.42) * mm, "end": v(-45.45, 42.63) * mm});
            skLineSegment(sketch, "E142", {"start": v(-45.45, 42.63) * mm, "end": v(-45.44, 42.77) * mm});
            skLineSegment(sketch, "E143", {"start": v(-45.44, 42.77) * mm, "end": v(-45.43, 42.88) * mm});
            skLineSegment(sketch, "E144", {"start": v(-45.43, 42.88) * mm, "end": v(-45.4, 43) * mm});
            skLineSegment(sketch, "E145", {"start": v(-45.4, 43) * mm, "end": v(-45.15, 43.7) * mm});
            skLineSegment(sketch, "E146", {"start": v(-45.15, 43.7) * mm, "end": v(-44.72, 44.29) * mm});
            skLineSegment(sketch, "E147", {"start": v(-44.72, 44.29) * mm, "end": v(-44.15, 44.71) * mm});
            skLineSegment(sketch, "E148", {"start": v(-44.15, 44.71) * mm, "end": v(-43.47, 44.95) * mm});
            skLineSegment(sketch, "E149", {"start": v(-43.47, 44.95) * mm, "end": v(-43.24, 44.98) * mm});
            skLineSegment(sketch, "E150", {"start": v(-43.24, 44.98) * mm, "end": v(-42.95, 44.98) * mm});
            skLineSegment(sketch, "E151", {"start": v(-42.95, 44.98) * mm, "end": v(-42.66, 44.97) * mm});
            skLineSegment(sketch, "E152", {"start": v(-42.66, 44.97) * mm, "end": v(-42.42, 44.94) * mm});
            skLineSegment(sketch, "E153", {"start": v(-42.42, 44.94) * mm, "end": v(-41.75, 44.7) * mm});
            skLineSegment(sketch, "E154", {"start": v(-41.75, 44.7) * mm, "end": v(-41.22, 44.3) * mm});
            skLineSegment(sketch, "E155", {"start": v(-41.22, 44.3) * mm, "end": v(-40.83, 43.74) * mm});
            skLineSegment(sketch, "E156", {"start": v(-40.83, 43.74) * mm, "end": v(-40.59, 43.03) * mm});
            skLineSegment(sketch, "E157", {"start": v(-40.59, 43.03) * mm, "end": v(-40.56, 42.8) * mm});
            skLineSegment(sketch, "E158", {"start": v(-40.56, 42.8) * mm, "end": v(-40.53, 42.54) * mm});
            skLineSegment(sketch, "E159", {"start": v(-40.53, 42.54) * mm, "end": v(-40.52, 42.29) * mm});
            skLineSegment(sketch, "E160", {"start": v(-40.52, 42.29) * mm, "end": v(-40.52, 42.1) * mm});
            skLineSegment(sketch, "E161", {"start": v(-40.52, 42.1) * mm, "end": v(-40.54, 41.95) * mm});
            skLineSegment(sketch, "E162", {"start": v(-40.54, 41.95) * mm, "end": v(-43.79, 41.95) * mm});
            skLineSegment(sketch, "E163", {"start": v(-43.79, 41.95) * mm, "end": v(-43.78, 41.9) * mm});
            skLineSegment(sketch, "E164", {"start": v(-43.78, 41.9) * mm, "end": v(-43.75, 41.83) * mm});
            skLineSegment(sketch, "E165", {"start": v(-43.75, 41.83) * mm, "end": v(-43.7, 41.73) * mm});
            skLineSegment(sketch, "E166", {"start": v(-43.7, 41.73) * mm, "end": v(-43.6, 41.55) * mm});
            skLineSegment(sketch, "E167", {"start": v(-43.6, 41.55) * mm, "end": v(-43.44, 41.4) * mm});
            skLineSegment(sketch, "E168", {"start": v(-43.44, 41.4) * mm, "end": v(-43.25, 41.28) * mm});
            skLineSegment(sketch, "E169", {"start": v(-43.25, 41.28) * mm, "end": v(-43.04, 41.2) * mm});
            skLineSegment(sketch, "E170", {"start": v(-43.04, 41.2) * mm, "end": v(-42.87, 41.18) * mm});
            skLineSegment(sketch, "E171", {"start": v(-42.87, 41.18) * mm, "end": v(-42.68, 41.18) * mm});
            skLineSegment(sketch, "E172", {"start": v(-42.68, 41.18) * mm, "end": v(-42.48, 41.2) * mm});
            skLineSegment(sketch, "E173", {"start": v(-42.48, 41.2) * mm, "end": v(-42.32, 41.24) * mm});
            skLineSegment(sketch, "E174", {"start": v(-42.32, 41.24) * mm, "end": v(-42.06, 41.37) * mm});
            skLineSegment(sketch, "E175", {"start": v(-42.06, 41.37) * mm, "end": v(-41.8, 41.56) * mm});
            skLineSegment(sketch, "E176", {"start": v(-41.8, 41.56) * mm, "end": v(-41.67, 41.67) * mm});
            skLineSegment(sketch, "E177", {"start": v(-41.67, 41.67) * mm, "end": v(-41.18, 41.27) * mm});
            skLineSegment(sketch, "E178", {"start": v(-41.18, 41.27) * mm, "end": v(-40.7, 40.87) * mm});
            skLineSegment(sketch, "E179", {"start": v(-40.7, 40.87) * mm, "end": v(-40.8, 40.77) * mm});
            skLineSegment(sketch, "E180", {"start": v(-40.8, 40.77) * mm, "end": v(-41.4, 40.25) * mm});
            skLineSegment(sketch, "E181", {"start": v(-41.4, 40.25) * mm, "end": v(-42.17, 39.94) * mm});
            skLineSegment(sketch, "E182", {"start": v(-42.17, 39.94) * mm, "end": v(-42.29, 39.92) * mm});
            skLineSegment(sketch, "E183", {"start": v(-42.29, 39.92) * mm, "end": v(-42.4, 39.9) * mm});
            skLineSegment(sketch, "E184", {"start": v(-42.4, 39.9) * mm, "end": v(-42.56, 39.9) * mm});
            skLineSegment(sketch, "E185", {"start": v(-42.56, 39.9) * mm, "end": v(-42.78, 39.9) * mm});
            skLineSegment(sketch, "E186", {"start": v(-42.78, 39.9) * mm, "end": v(-42.94, 39.9) * mm});
            skLineSegment(sketch, "E187", {"start": v(-42.94, 39.9) * mm, "end": v(-43.1, 39.9) * mm});
            skLineSegment(sketch, "E188", {"start": v(-43.1, 39.9) * mm, "end": v(-43.2, 39.9) * mm});
            skLineSegment(sketch, "E189", {"start": v(-43.2, 39.9) * mm, "end": v(-43.28, 39.9) * mm});
            skLineSegment(sketch, "E190", {"start": v(-43.28, 39.9) * mm, "end": v(-43.28, 39.9) * mm});
            skLineSegment(sketch, "E191", {"start": v(-42.15, 42.88) * mm, "end": v(-42.16, 42.95) * mm});
            skLineSegment(sketch, "E192", {"start": v(-42.16, 42.95) * mm, "end": v(-42.2, 43.05) * mm});
            skLineSegment(sketch, "E193", {"start": v(-42.2, 43.05) * mm, "end": v(-42.23, 43.17) * mm});
            skLineSegment(sketch, "E194", {"start": v(-42.23, 43.17) * mm, "end": v(-42.27, 43.27) * mm});
            skLineSegment(sketch, "E195", {"start": v(-42.27, 43.27) * mm, "end": v(-42.42, 43.48) * mm});
            skLineSegment(sketch, "E196", {"start": v(-42.42, 43.48) * mm, "end": v(-42.62, 43.63) * mm});
            skLineSegment(sketch, "E197", {"start": v(-42.62, 43.63) * mm, "end": v(-42.86, 43.7) * mm});
            skLineSegment(sketch, "E198", {"start": v(-42.86, 43.7) * mm, "end": v(-43.11, 43.7) * mm});
            skLineSegment(sketch, "E199", {"start": v(-43.11, 43.7) * mm, "end": v(-43.34, 43.62) * mm});
            skLineSegment(sketch, "E200", {"start": v(-43.34, 43.62) * mm, "end": v(-43.53, 43.47) * mm});
            skLineSegment(sketch, "E201", {"start": v(-43.53, 43.47) * mm, "end": v(-43.68, 43.26) * mm});
            skLineSegment(sketch, "E202", {"start": v(-43.68, 43.26) * mm, "end": v(-43.79, 43) * mm});
            skLineSegment(sketch, "E203", {"start": v(-43.79, 43) * mm, "end": v(-43.82, 42.85) * mm});
            skLineSegment(sketch, "E204", {"start": v(-43.82, 42.85) * mm, "end": v(-42.99, 42.85) * mm});
            skLineSegment(sketch, "E205", {"start": v(-42.99, 42.85) * mm, "end": v(-42.73, 42.85) * mm});
            skLineSegment(sketch, "E206", {"start": v(-42.73, 42.85) * mm, "end": v(-42.54, 42.85) * mm});
            skLineSegment(sketch, "E207", {"start": v(-42.54, 42.85) * mm, "end": v(-42.39, 42.86) * mm});
            skLineSegment(sketch, "E208", {"start": v(-42.39, 42.86) * mm, "end": v(-42.28, 42.86) * mm});
            skLineSegment(sketch, "E209", {"start": v(-42.28, 42.86) * mm, "end": v(-42.21, 42.86) * mm});
            skLineSegment(sketch, "E210", {"start": v(-42.21, 42.86) * mm, "end": v(-42.17, 42.86) * mm});
            skLineSegment(sketch, "E211", {"start": v(-42.17, 42.86) * mm, "end": v(-42.15, 42.87) * mm});
            skLineSegment(sketch, "E212", {"start": v(-42.15, 42.87) * mm, "end": v(-42.15, 42.88) * mm});
            skLineSegment(sketch, "E213", {"start": v(-42.15, 42.88) * mm, "end": v(-42.15, 42.88) * mm});
            skLineSegment(sketch, "E214", {"start": v(-40.19, 41.72) * mm, "end": v(-40.19, 44.88) * mm});
            skLineSegment(sketch, "E215", {"start": v(-40.19, 44.88) * mm, "end": v(-38.46, 44.88) * mm});
            skLineSegment(sketch, "E216", {"start": v(-38.46, 44.88) * mm, "end": v(-38.46, 44.25) * mm});
            skLineSegment(sketch, "E217", {"start": v(-38.46, 44.25) * mm, "end": v(-38.3, 44.42) * mm});
            skLineSegment(sketch, "E218", {"start": v(-38.3, 44.42) * mm, "end": v(-38.02, 44.66) * mm});
            skLineSegment(sketch, "E219", {"start": v(-38.02, 44.66) * mm, "end": v(-37.74, 44.83) * mm});
            skLineSegment(sketch, "E220", {"start": v(-37.74, 44.83) * mm, "end": v(-37.43, 44.94) * mm});
            skLineSegment(sketch, "E221", {"start": v(-37.43, 44.94) * mm, "end": v(-37.08, 44.99) * mm});
            skLineSegment(sketch, "E222", {"start": v(-37.08, 44.99) * mm, "end": v(-36.37, 44.9) * mm});
            skLineSegment(sketch, "E223", {"start": v(-36.37, 44.9) * mm, "end": v(-35.75, 44.57) * mm});
            skLineSegment(sketch, "E224", {"start": v(-35.75, 44.57) * mm, "end": v(-35.26, 44.04) * mm});
            skLineSegment(sketch, "E225", {"start": v(-35.26, 44.04) * mm, "end": v(-34.94, 43.35) * mm});
            skLineSegment(sketch, "E226", {"start": v(-34.94, 43.35) * mm, "end": v(-34.82, 42.57) * mm});
            skLineSegment(sketch, "E227", {"start": v(-34.82, 42.57) * mm, "end": v(-34.88, 41.76) * mm});
            skLineSegment(sketch, "E228", {"start": v(-34.88, 41.76) * mm, "end": v(-35.1, 41.12) * mm});
            skLineSegment(sketch, "E229", {"start": v(-35.1, 41.12) * mm, "end": v(-35.44, 40.6) * mm});
            skLineSegment(sketch, "E230", {"start": v(-35.44, 40.6) * mm, "end": v(-35.91, 40.19) * mm});
            skLineSegment(sketch, "E231", {"start": v(-35.91, 40.19) * mm, "end": v(-36.47, 39.94) * mm});
            skLineSegment(sketch, "E232", {"start": v(-36.47, 39.94) * mm, "end": v(-36.59, 39.92) * mm});
            skLineSegment(sketch, "E233", {"start": v(-36.59, 39.92) * mm, "end": v(-36.69, 39.9) * mm});
            skLineSegment(sketch, "E234", {"start": v(-36.69, 39.9) * mm, "end": v(-36.8, 39.9) * mm});
            skLineSegment(sketch, "E235", {"start": v(-36.8, 39.9) * mm, "end": v(-36.98, 39.9) * mm});
            skLineSegment(sketch, "E236", {"start": v(-36.98, 39.9) * mm, "end": v(-37.16, 39.9) * mm});
            skLineSegment(sketch, "E237", {"start": v(-37.16, 39.9) * mm, "end": v(-37.28, 39.9) * mm});
            skLineSegment(sketch, "E238", {"start": v(-37.28, 39.9) * mm, "end": v(-37.38, 39.92) * mm});
            skLineSegment(sketch, "E239", {"start": v(-37.38, 39.92) * mm, "end": v(-37.48, 39.94) * mm});
            skLineSegment(sketch, "E240", {"start": v(-37.48, 39.94) * mm, "end": v(-37.71, 40.02) * mm});
            skLineSegment(sketch, "E241", {"start": v(-37.71, 40.02) * mm, "end": v(-37.92, 40.12) * mm});
            skLineSegment(sketch, "E242", {"start": v(-37.92, 40.12) * mm, "end": v(-38.12, 40.26) * mm});
            skLineSegment(sketch, "E243", {"start": v(-38.12, 40.26) * mm, "end": v(-38.32, 40.43) * mm});
            skLineSegment(sketch, "E244", {"start": v(-38.32, 40.43) * mm, "end": v(-38.46, 40.56) * mm});
            skLineSegment(sketch, "E245", {"start": v(-38.46, 40.56) * mm, "end": v(-38.46, 38.54) * mm});
            skLineSegment(sketch, "E246", {"start": v(-38.46, 38.54) * mm, "end": v(-40.19, 38.54) * mm});
            skLineSegment(sketch, "E247", {"start": v(-40.19, 38.54) * mm, "end": v(-40.19, 41.72) * mm});
            skLineSegment(sketch, "E248", {"start": v(-40.19, 41.72) * mm, "end": v(-40.19, 41.72) * mm});
            skLineSegment(sketch, "E249", {"start": v(-37.34, 41.35) * mm, "end": v(-37.15, 41.4) * mm});
            skLineSegment(sketch, "E250", {"start": v(-37.15, 41.4) * mm, "end": v(-36.95, 41.52) * mm});
            skLineSegment(sketch, "E251", {"start": v(-36.95, 41.52) * mm, "end": v(-36.79, 41.67) * mm});
            skLineSegment(sketch, "E252", {"start": v(-36.79, 41.67) * mm, "end": v(-36.66, 41.84) * mm});
            skLineSegment(sketch, "E253", {"start": v(-36.66, 41.84) * mm, "end": v(-36.57, 42.06) * mm});
            skLineSegment(sketch, "E254", {"start": v(-36.57, 42.06) * mm, "end": v(-36.53, 42.3) * mm});
            skLineSegment(sketch, "E255", {"start": v(-36.53, 42.3) * mm, "end": v(-36.53, 42.53) * mm});
            skLineSegment(sketch, "E256", {"start": v(-36.53, 42.53) * mm, "end": v(-36.57, 42.76) * mm});
            skLineSegment(sketch, "E257", {"start": v(-36.57, 42.76) * mm, "end": v(-36.72, 43.1) * mm});
            skLineSegment(sketch, "E258", {"start": v(-36.72, 43.1) * mm, "end": v(-36.97, 43.37) * mm});
            skLineSegment(sketch, "E259", {"start": v(-36.97, 43.37) * mm, "end": v(-37.28, 43.51) * mm});
            skLineSegment(sketch, "E260", {"start": v(-37.28, 43.51) * mm, "end": v(-37.64, 43.53) * mm});
            skLineSegment(sketch, "E261", {"start": v(-37.64, 43.53) * mm, "end": v(-37.91, 43.44) * mm});
            skLineSegment(sketch, "E262", {"start": v(-37.91, 43.44) * mm, "end": v(-38.15, 43.27) * mm});
            skLineSegment(sketch, "E263", {"start": v(-38.15, 43.27) * mm, "end": v(-38.33, 43.04) * mm});
            skLineSegment(sketch, "E264", {"start": v(-38.33, 43.04) * mm, "end": v(-38.45, 42.75) * mm});
            skLineSegment(sketch, "E265", {"start": v(-38.45, 42.75) * mm, "end": v(-38.47, 42.61) * mm});
            skLineSegment(sketch, "E266", {"start": v(-38.47, 42.61) * mm, "end": v(-38.48, 42.44) * mm});
            skLineSegment(sketch, "E267", {"start": v(-38.48, 42.44) * mm, "end": v(-38.47, 42.27) * mm});
            skLineSegment(sketch, "E268", {"start": v(-38.47, 42.27) * mm, "end": v(-38.45, 42.13) * mm});
            skLineSegment(sketch, "E269", {"start": v(-38.45, 42.13) * mm, "end": v(-38.34, 41.85) * mm});
            skLineSegment(sketch, "E270", {"start": v(-38.34, 41.85) * mm, "end": v(-38.17, 41.62) * mm});
            skLineSegment(sketch, "E271", {"start": v(-38.17, 41.62) * mm, "end": v(-37.95, 41.45) * mm});
            skLineSegment(sketch, "E272", {"start": v(-37.95, 41.45) * mm, "end": v(-37.7, 41.35) * mm});
            skLineSegment(sketch, "E273", {"start": v(-37.7, 41.35) * mm, "end": v(-37.53, 41.33) * mm});
            skLineSegment(sketch, "E274", {"start": v(-37.53, 41.33) * mm, "end": v(-37.34, 41.35) * mm});
            skLineSegment(sketch, "E275", {"start": v(-28.9, 42.44) * mm, "end": v(-28.9, 44.88) * mm});
            skLineSegment(sketch, "E276", {"start": v(-28.9, 44.88) * mm, "end": v(-27.16, 44.88) * mm});
            skLineSegment(sketch, "E277", {"start": v(-27.16, 44.88) * mm, "end": v(-27.16, 40) * mm});
            skLineSegment(sketch, "E278", {"start": v(-27.16, 40) * mm, "end": v(-28.9, 40) * mm});
            skLineSegment(sketch, "E279", {"start": v(-28.9, 40) * mm, "end": v(-28.9, 42.44) * mm});
            skLineSegment(sketch, "E280", {"start": v(-32.41, 39.93) * mm, "end": v(-33.2, 40.17) * mm});
            skLineSegment(sketch, "E281", {"start": v(-33.2, 40.17) * mm, "end": v(-33.84, 40.6) * mm});
            skLineSegment(sketch, "E282", {"start": v(-33.84, 40.6) * mm, "end": v(-34.31, 41.2) * mm});
            skLineSegment(sketch, "E283", {"start": v(-34.31, 41.2) * mm, "end": v(-34.6, 41.94) * mm});
            skLineSegment(sketch, "E284", {"start": v(-34.6, 41.94) * mm, "end": v(-34.63, 42.13) * mm});
            skLineSegment(sketch, "E285", {"start": v(-34.63, 42.13) * mm, "end": v(-34.64, 42.37) * mm});
            skLineSegment(sketch, "E286", {"start": v(-34.64, 42.37) * mm, "end": v(-34.64, 42.62) * mm});
            skLineSegment(sketch, "E287", {"start": v(-34.65, 42.42) * mm, "end": v(-34.64, 42.62) * mm});
            skLineSegment(sketch, "E288", {"start": v(-34.62, 42.83) * mm, "end": v(-34.36, 43.6) * mm});
            skLineSegment(sketch, "E289", {"start": v(-34.36, 43.6) * mm, "end": v(-33.86, 44.26) * mm});
            skLineSegment(sketch, "E290", {"start": v(-33.86, 44.26) * mm, "end": v(-33.48, 44.57) * mm});
            skLineSegment(sketch, "E291", {"start": v(-33.48, 44.57) * mm, "end": v(-33.05, 44.8) * mm});
            skLineSegment(sketch, "E292", {"start": v(-33.05, 44.8) * mm, "end": v(-32.58, 44.94) * mm});
            skLineSegment(sketch, "E293", {"start": v(-32.58, 44.94) * mm, "end": v(-32.07, 45) * mm});
            skLineSegment(sketch, "E294", {"start": v(-32.07, 45) * mm, "end": v(-31.49, 44.98) * mm});
            skLineSegment(sketch, "E295", {"start": v(-31.49, 44.98) * mm, "end": v(-30.94, 44.84) * mm});
            skLineSegment(sketch, "E296", {"start": v(-30.94, 44.84) * mm, "end": v(-30.44, 44.6) * mm});
            skLineSegment(sketch, "E297", {"start": v(-30.44, 44.6) * mm, "end": v(-30, 44.26) * mm});
            skLineSegment(sketch, "E298", {"start": v(-30, 44.26) * mm, "end": v(-29.53, 43.63) * mm});
            skLineSegment(sketch, "E299", {"start": v(-29.53, 43.63) * mm, "end": v(-29.27, 42.9) * mm});
            skLineSegment(sketch, "E300", {"start": v(-29.27, 42.9) * mm, "end": v(-29.25, 42.7) * mm});
            skLineSegment(sketch, "E301", {"start": v(-29.25, 42.7) * mm, "end": v(-29.24, 42.45) * mm});
            skLineSegment(sketch, "E302", {"start": v(-29.24, 42.45) * mm, "end": v(-29.26, 42.2) * mm});
            skLineSegment(sketch, "E303", {"start": v(-29.26, 42.2) * mm, "end": v(-29.29, 42) * mm});
            skLineSegment(sketch, "E304", {"start": v(-29.29, 42) * mm, "end": v(-29.55, 41.25) * mm});
            skLineSegment(sketch, "E305", {"start": v(-29.55, 41.25) * mm, "end": v(-30.03, 40.64) * mm});
            skLineSegment(sketch, "E306", {"start": v(-30.03, 40.64) * mm, "end": v(-30.67, 40.19) * mm});
            skLineSegment(sketch, "E307", {"start": v(-30.67, 40.19) * mm, "end": v(-31.44, 39.94) * mm});
            skLineSegment(sketch, "E308", {"start": v(-31.44, 39.94) * mm, "end": v(-31.93, 39.9) * mm});
            skLineSegment(sketch, "E309", {"start": v(-31.93, 39.9) * mm, "end": v(-32.41, 39.93) * mm});
            skLineSegment(sketch, "E310", {"start": v(-31.68, 41.4) * mm, "end": v(-31.45, 41.5) * mm});
            skLineSegment(sketch, "E311", {"start": v(-31.45, 41.5) * mm, "end": v(-31.26, 41.63) * mm});
            skLineSegment(sketch, "E312", {"start": v(-31.26, 41.63) * mm, "end": v(-31.1, 41.82) * mm});
            skLineSegment(sketch, "E313", {"start": v(-31.1, 41.82) * mm, "end": v(-31, 42.06) * mm});
            skLineSegment(sketch, "E314", {"start": v(-31, 42.06) * mm, "end": v(-30.93, 42.42) * mm});
            skLineSegment(sketch, "E315", {"start": v(-30.93, 42.42) * mm, "end": v(-30.97, 42.77) * mm});
            skLineSegment(sketch, "E316", {"start": v(-30.97, 42.77) * mm, "end": v(-31.1, 43.04) * mm});
            skLineSegment(sketch, "E317", {"start": v(-31.1, 43.04) * mm, "end": v(-31.27, 43.26) * mm});
            skLineSegment(sketch, "E318", {"start": v(-31.27, 43.26) * mm, "end": v(-31.5, 43.42) * mm});
            skLineSegment(sketch, "E319", {"start": v(-31.5, 43.42) * mm, "end": v(-31.76, 43.52) * mm});
            skLineSegment(sketch, "E320", {"start": v(-31.76, 43.52) * mm, "end": v(-31.87, 43.54) * mm});
            skLineSegment(sketch, "E321", {"start": v(-31.87, 43.54) * mm, "end": v(-31.96, 43.55) * mm});
            skLineSegment(sketch, "E322", {"start": v(-31.96, 43.55) * mm, "end": v(-32.18, 43.52) * mm});
            skLineSegment(sketch, "E323", {"start": v(-32.18, 43.52) * mm, "end": v(-32.4, 43.44) * mm});
            skLineSegment(sketch, "E324", {"start": v(-32.4, 43.44) * mm, "end": v(-32.58, 43.32) * mm});
            skLineSegment(sketch, "E325", {"start": v(-32.58, 43.32) * mm, "end": v(-32.73, 43.16) * mm});
            skLineSegment(sketch, "E326", {"start": v(-32.73, 43.16) * mm, "end": v(-32.85, 42.97) * mm});
            skLineSegment(sketch, "E327", {"start": v(-32.85, 42.97) * mm, "end": v(-32.92, 42.76) * mm});
            skLineSegment(sketch, "E328", {"start": v(-32.92, 42.76) * mm, "end": v(-32.95, 42.62) * mm});
            skLineSegment(sketch, "E329", {"start": v(-32.95, 42.62) * mm, "end": v(-32.95, 42.46) * mm});
            skLineSegment(sketch, "E330", {"start": v(-32.95, 42.46) * mm, "end": v(-32.95, 42.3) * mm});
            skLineSegment(sketch, "E331", {"start": v(-32.95, 42.3) * mm, "end": v(-32.92, 42.18) * mm});
            skLineSegment(sketch, "E332", {"start": v(-32.92, 42.18) * mm, "end": v(-32.82, 41.9) * mm});
            skLineSegment(sketch, "E333", {"start": v(-32.82, 41.9) * mm, "end": v(-32.65, 41.68) * mm});
            skLineSegment(sketch, "E334", {"start": v(-32.65, 41.68) * mm, "end": v(-32.44, 41.5) * mm});
            skLineSegment(sketch, "E335", {"start": v(-32.44, 41.5) * mm, "end": v(-32.19, 41.4) * mm});
            skLineSegment(sketch, "E336", {"start": v(-32.19, 41.4) * mm, "end": v(-31.94, 41.37) * mm});
            skLineSegment(sketch, "E337", {"start": v(-31.94, 41.37) * mm, "end": v(-31.68, 41.4) * mm});
            skLineSegment(sketch, "E338", {"start": v(-31.68, 41.4) * mm, "end": v(-31.68, 41.4) * mm});
            skLineSegment(sketch, "E339", {"start": v(-26.6, 42.44) * mm, "end": v(-26.6, 44.88) * mm});
            skLineSegment(sketch, "E340", {"start": v(-26.6, 44.88) * mm, "end": v(-24.86, 44.88) * mm});
            skLineSegment(sketch, "E341", {"start": v(-24.86, 44.88) * mm, "end": v(-24.86, 44.23) * mm});
            skLineSegment(sketch, "E342", {"start": v(-24.86, 44.23) * mm, "end": v(-24.68, 44.41) * mm});
            skLineSegment(sketch, "E343", {"start": v(-24.68, 44.41) * mm, "end": v(-24.33, 44.71) * mm});
            skLineSegment(sketch, "E344", {"start": v(-24.33, 44.71) * mm, "end": v(-23.96, 44.9) * mm});
            skLineSegment(sketch, "E345", {"start": v(-23.96, 44.9) * mm, "end": v(-23.55, 45) * mm});
            skLineSegment(sketch, "E346", {"start": v(-23.55, 45) * mm, "end": v(-23.12, 44.97) * mm});
            skLineSegment(sketch, "E347", {"start": v(-23.12, 44.97) * mm, "end": v(-22.6, 44.82) * mm});
            skLineSegment(sketch, "E348", {"start": v(-22.6, 44.82) * mm, "end": v(-22.2, 44.52) * mm});
            skLineSegment(sketch, "E349", {"start": v(-22.2, 44.52) * mm, "end": v(-21.91, 44.08) * mm});
            skLineSegment(sketch, "E350", {"start": v(-21.91, 44.08) * mm, "end": v(-21.76, 43.53) * mm});
            skLineSegment(sketch, "E351", {"start": v(-21.76, 43.53) * mm, "end": v(-21.76, 43.35) * mm});
            skLineSegment(sketch, "E352", {"start": v(-21.76, 43.35) * mm, "end": v(-21.75, 42.95) * mm});
            skLineSegment(sketch, "E353", {"start": v(-21.75, 42.95) * mm, "end": v(-21.74, 42.39) * mm});
            skLineSegment(sketch, "E354", {"start": v(-21.74, 42.39) * mm, "end": v(-21.74, 41.7) * mm});
            skLineSegment(sketch, "E355", {"start": v(-21.74, 41.7) * mm, "end": v(-21.74, 40) * mm});
            skLineSegment(sketch, "E356", {"start": v(-21.74, 40) * mm, "end": v(-23.47, 40) * mm});
            skLineSegment(sketch, "E357", {"start": v(-23.47, 40) * mm, "end": v(-23.47, 41.39) * mm});
            skLineSegment(sketch, "E358", {"start": v(-23.47, 41.39) * mm, "end": v(-23.47, 41.89) * mm});
            skLineSegment(sketch, "E359", {"start": v(-23.47, 41.89) * mm, "end": v(-23.47, 42.27) * mm});
            skLineSegment(sketch, "E360", {"start": v(-23.47, 42.27) * mm, "end": v(-23.48, 42.55) * mm});
            skLineSegment(sketch, "E361", {"start": v(-23.48, 42.55) * mm, "end": v(-23.49, 42.75) * mm});
            skLineSegment(sketch, "E362", {"start": v(-23.49, 42.75) * mm, "end": v(-23.5, 42.89) * mm});
            skLineSegment(sketch, "E363", {"start": v(-23.5, 42.89) * mm, "end": v(-23.52, 42.98) * mm});
            skLineSegment(sketch, "E364", {"start": v(-23.52, 42.98) * mm, "end": v(-23.54, 43.05) * mm});
            skLineSegment(sketch, "E365", {"start": v(-23.54, 43.05) * mm, "end": v(-23.58, 43.12) * mm});
            skLineSegment(sketch, "E366", {"start": v(-23.58, 43.12) * mm, "end": v(-23.73, 43.31) * mm});
            skLineSegment(sketch, "E367", {"start": v(-23.73, 43.31) * mm, "end": v(-23.95, 43.43) * mm});
            skLineSegment(sketch, "E368", {"start": v(-23.95, 43.43) * mm, "end": v(-24.2, 43.46) * mm});
            skLineSegment(sketch, "E369", {"start": v(-24.2, 43.46) * mm, "end": v(-24.45, 43.4) * mm});
            skLineSegment(sketch, "E370", {"start": v(-24.45, 43.4) * mm, "end": v(-24.63, 43.26) * mm});
            skLineSegment(sketch, "E371", {"start": v(-24.63, 43.26) * mm, "end": v(-24.77, 43.07) * mm});
            skLineSegment(sketch, "E372", {"start": v(-24.77, 43.07) * mm, "end": v(-24.8, 43) * mm});
            skLineSegment(sketch, "E373", {"start": v(-24.8, 43) * mm, "end": v(-24.82, 42.93) * mm});
            skLineSegment(sketch, "E374", {"start": v(-24.82, 42.93) * mm, "end": v(-24.84, 42.83) * mm});
            skLineSegment(sketch, "E375", {"start": v(-24.84, 42.83) * mm, "end": v(-24.85, 42.7) * mm});
            skLineSegment(sketch, "E376", {"start": v(-24.85, 42.7) * mm, "end": v(-24.86, 42.5) * mm});
            skLineSegment(sketch, "E377", {"start": v(-24.86, 42.5) * mm, "end": v(-24.86, 42.22) * mm});
            skLineSegment(sketch, "E378", {"start": v(-24.86, 42.22) * mm, "end": v(-24.86, 41.85) * mm});
            skLineSegment(sketch, "E379", {"start": v(-24.86, 41.85) * mm, "end": v(-24.86, 41.36) * mm});
            skLineSegment(sketch, "E380", {"start": v(-24.86, 41.36) * mm, "end": v(-24.86, 40) * mm});
            skLineSegment(sketch, "E381", {"start": v(-24.86, 40) * mm, "end": v(-26.6, 40) * mm});
            skLineSegment(sketch, "E382", {"start": v(-26.6, 40) * mm, "end": v(-26.6, 42.44) * mm});
            skLineSegment(sketch, "E383", {"start": v(-26.6, 42.44) * mm, "end": v(-26.6, 42.44) * mm});
            skLineSegment(sketch, "E384", {"start": v(-20.9, 41.78) * mm, "end": v(-20.9, 43.53) * mm});
            skLineSegment(sketch, "E385", {"start": v(-20.9, 43.53) * mm, "end": v(-21.49, 43.53) * mm});
            skLineSegment(sketch, "E386", {"start": v(-21.49, 43.53) * mm, "end": v(-21.49, 44.92) * mm});
            skLineSegment(sketch, "E387", {"start": v(-21.49, 44.92) * mm, "end": v(-20.9, 44.92) * mm});
            skLineSegment(sketch, "E388", {"start": v(-20.9, 44.92) * mm, "end": v(-20.9, 46.16) * mm});
            skLineSegment(sketch, "E389", {"start": v(-20.9, 46.16) * mm, "end": v(-19.17, 46.16) * mm});
            skLineSegment(sketch, "E390", {"start": v(-19.17, 46.16) * mm, "end": v(-19.17, 44.92) * mm});
            skLineSegment(sketch, "E391", {"start": v(-19.17, 44.92) * mm, "end": v(-18.05, 44.92) * mm});
            skLineSegment(sketch, "E392", {"start": v(-18.05, 44.92) * mm, "end": v(-18.05, 43.53) * mm});
            skLineSegment(sketch, "E393", {"start": v(-18.05, 43.53) * mm, "end": v(-19.17, 43.53) * mm});
            skLineSegment(sketch, "E394", {"start": v(-19.17, 43.53) * mm, "end": v(-19.17, 40.03) * mm});
            skLineSegment(sketch, "E395", {"start": v(-19.17, 40.03) * mm, "end": v(-20.9, 40.03) * mm});
            skLineSegment(sketch, "E396", {"start": v(-20.9, 40.03) * mm, "end": v(-20.9, 41.78) * mm});
            skLineSegment(sketch, "E397", {"start": v(-17.67, 40.02) * mm, "end": v(-17.94, 40.14) * mm});
            skLineSegment(sketch, "E398", {"start": v(-17.94, 40.14) * mm, "end": v(-18.17, 40.33) * mm});
            skLineSegment(sketch, "E399", {"start": v(-18.17, 40.33) * mm, "end": v(-18.34, 40.56) * mm});
            skLineSegment(sketch, "E400", {"start": v(-18.34, 40.56) * mm, "end": v(-18.44, 40.84) * mm});
            skLineSegment(sketch, "E401", {"start": v(-18.44, 40.84) * mm, "end": v(-18.45, 40.97) * mm});
            skLineSegment(sketch, "E402", {"start": v(-18.45, 40.97) * mm, "end": v(-18.45, 41.13) * mm});
            skLineSegment(sketch, "E403", {"start": v(-18.45, 41.13) * mm, "end": v(-18.43, 41.27) * mm});
            skLineSegment(sketch, "E404", {"start": v(-18.43, 41.27) * mm, "end": v(-18.4, 41.4) * mm});
            skLineSegment(sketch, "E405", {"start": v(-18.4, 41.4) * mm, "end": v(-18.28, 41.62) * mm});
            skLineSegment(sketch, "E406", {"start": v(-18.28, 41.62) * mm, "end": v(-18.13, 41.8) * mm});
            skLineSegment(sketch, "E407", {"start": v(-18.13, 41.8) * mm, "end": v(-17.93, 41.96) * mm});
            skLineSegment(sketch, "E408", {"start": v(-17.93, 41.96) * mm, "end": v(-17.7, 42.06) * mm});
            skLineSegment(sketch, "E409", {"start": v(-17.7, 42.06) * mm, "end": v(-17.56, 42.09) * mm});
            skLineSegment(sketch, "E410", {"start": v(-17.56, 42.09) * mm, "end": v(-17.4, 42.1) * mm});
            skLineSegment(sketch, "E411", {"start": v(-17.4, 42.1) * mm, "end": v(-17.23, 42.09) * mm});
            skLineSegment(sketch, "E412", {"start": v(-17.23, 42.09) * mm, "end": v(-17.1, 42.06) * mm});
            skLineSegment(sketch, "E413", {"start": v(-17.1, 42.06) * mm, "end": v(-16.78, 41.9) * mm});
            skLineSegment(sketch, "E414", {"start": v(-16.78, 41.9) * mm, "end": v(-16.54, 41.67) * mm});
            skLineSegment(sketch, "E415", {"start": v(-16.54, 41.67) * mm, "end": v(-16.4, 41.38) * mm});
            skLineSegment(sketch, "E416", {"start": v(-16.4, 41.38) * mm, "end": v(-16.35, 41.07) * mm});
            skLineSegment(sketch, "E417", {"start": v(-16.4, 40.7) * mm, "end": v(-16.56, 40.4) * mm});
            skLineSegment(sketch, "E418", {"start": v(-16.56, 40.4) * mm, "end": v(-16.81, 40.16) * mm});
            skLineSegment(sketch, "E419", {"start": v(-16.81, 40.16) * mm, "end": v(-17.12, 40.02) * mm});
            skLineSegment(sketch, "E420", {"start": v(-17.12, 40.02) * mm, "end": v(-17.25, 40) * mm});
            skLineSegment(sketch, "E421", {"start": v(-17.25, 40) * mm, "end": v(-17.4, 40) * mm});
            skLineSegment(sketch, "E422", {"start": v(-17.4, 40) * mm, "end": v(-17.55, 40) * mm});
            skLineSegment(sketch, "E423", {"start": v(-17.55, 40) * mm, "end": v(-17.67, 40.02) * mm});
            skLineSegment(sketch, "E424", {"start": v(-17.67, 40.02) * mm, "end": v(-17.67, 40.02) * mm});
            skLineSegment(sketch, "E425", {"start": v(-56.34, 42.62) * mm, "end": v(-56.34, 42.37) * mm});
            skLineSegment(sketch, "E426", {"start": v(-16.35, 41.07) * mm, "end": v(-16.35, 40.88) * mm});
            skLineSegment(sketch, "E427", {"start": v(-16.35, 40.88) * mm, "end": v(-16.4, 40.7) * mm});
            skPoint(sketch, "E428.middle", {"position": v(-36.38, 42.42) * mm});
            skLineSegment(sketch, "E429", {"start": v(-34.62, 42.83) * mm, "end": v(-34.64, 42.62) * mm});
            skSolve(sketch);
        }
        {
            var Q0;
            Q0=qSketchRegion(id+"F15",true);
            extrude(context, id + "F16", {"entities" : qUnion([Q0]), "operationType" : NewBodyOperationType.ADD, "depth" : 1 * mm});
        }
        {
            var Q0;
            Q0=qCreatedBy(id+"F14.planeOp",FACE);
            cPlane(context, id + "F17", {"entities" : qUnion([Q0]), "cplaneType" : CPlaneType.OFFSET, "offset" : 7 * mm, "oppositeDirection" : true, "width" : 150 * mm, "height" : 150 * mm});
        }
        {
            var Q0;
            Q0=makeQuery(id+"F4.imprint","IMPRINT",FACE,{"disambiguationData":[TD([[makeQuery(id+"F4.imprint","IMPRINT",EDGE,{"derivedFrom":sQuery(id+"F4.wireOp",EDGE,"E15")}),1.0]])]});
            var Q1;
            Q1=sQuery(id+"F4.wireOp",EDGE,"E15");
            var Q2;
            {var subQ0=sQuery(id+"F0.wireOp",EDGE,"E6");Q2=makeQuery(id+"F1.opExtrude","SWEPT_FACE",FACE,{"disambiguationData":[OSD([subQ0]),TDD([makeQuery(id+"F0.imprint","IMPRINT",EDGE,{"disambiguationData":[TD([[makeQuery(id+"F0.imprint","INTERSECT",VERTEX,{"derivedFrom":[subQ0,sQuery(id+"F0.wireOp",EDGE,"E8")]}),1.0]])],"derivedFrom":subQ0})])]});}
            extrude(context, id + "F18", {"entities" : qUnion([Q0]), "operationType" : NewBodyOperationType.REMOVE, "surfaceEntities" : qUnion([Q1]), "endBound" : BoundingType.UP_TO_SURFACE, "endBoundEntityFace" : qUnion([Q2]), "depth" : 25 * mm});
        }
        {
            var Q0;
            Q0=makeQuery(id+"F18.boolean.opBoolean","COPY",EDGE,{"derivedFrom":makeQuery(id+"F18.opExtrude","CAP_EDGE",EDGE,{"disambiguationData":[OSD([sQuery(id+"F4.wireOp",EDGE,"E15")])],"isStart":false})});
            var Q1;
            Q1=makeQuery(id+"F18.boolean.opBoolean","INTERSECT",EDGE,{"derivedFrom":[makeQuery(id+"F1.opExtrude","SWEPT_FACE",FACE,{"disambiguationData":[OSD([sQuery(id+"F0.wireOp",EDGE,"E7")])]}),makeQuery(id+"F18.opExtrude","SWEPT_FACE",FACE,{"disambiguationData":[OSD([sQuery(id+"F4.wireOp",EDGE,"E15")])]})]});
            var Q2;
            Q2=makeQuery(id+"F8.boolean.opBoolean","COPY",EDGE,{"derivedFrom":makeQuery(id+"F8.opExtrude","TWEAK_EDGE",EDGE,{"derivedFrom":[makeQuery(id+"F1.opExtrude","SWEPT_FACE",FACE,{"disambiguationData":[OSD([sQuery(id+"F0.wireOp",EDGE,"E11")])]}),makeQuery(id+"F7.imprint","IMPRINT",EDGE,{"derivedFrom":sQuery(id+"F7.wireOp",EDGE,"E18.0.3.0")})]})});
            var Q3;
            Q3=makeQuery(id+"F5.boolean.opBoolean","COPY",EDGE,{"derivedFrom":makeQuery(id+"F5.opExtrude","CAP_EDGE",EDGE,{"disambiguationData":[OSD([sQuery(id+"F4.wireOp",EDGE,"E16.0.1.0")])],"isStart":false})});
            var Q4;
            Q4=makeQuery(id+"F12.boolean.opBoolean","INTERSECT",EDGE,{"derivedFrom":[makeQuery(id+"F1.opExtrude","SWEPT_FACE",FACE,{"disambiguationData":[OSD([sQuery(id+"F0.wireOp",EDGE,"E2")])]}),makeQuery(id+"F12.opExtrude","SWEPT_FACE",FACE,{"disambiguationData":[OSD([sQuery(id+"F11.wireOp",EDGE,"E19")])]})]});
            var Q5;
            Q5=makeQuery(id+"F12.boolean.opBoolean","INTERSECT",EDGE,{"derivedFrom":[makeQuery(id+"F1.opExtrude","SWEPT_FACE",FACE,{"disambiguationData":[OSD([sQuery(id+"F0.wireOp",EDGE,"E7")])]}),makeQuery(id+"F12.opExtrude","SWEPT_FACE",FACE,{"disambiguationData":[OSD([sQuery(id+"F11.wireOp",EDGE,"E19")])]})]});
            fillet(context, id + "F19", {"entities" : qUnion([Q0, Q1, Q2, Q3, Q4, Q5]), "radius" : 0.5 * mm, "tangentPropagation" : true, "allowEdgeOverflow" : false});
        }
        {
            var Q0;
            Q0=makeQuery(id+"F1.opExtrude","SWEPT_FACE",FACE,{"disambiguationData":[OSD([sQuery(id+"F0.wireOp",EDGE,"E4")])]});
            var sketch = newSketch(context, id + "F20", { "sketchPlane" : qUnion([Q0])});
            skText(sketch, "E430", { "text": "gop-labs.github.io", "fontName": "OpenSans-Bold.ttf"});
            const initialGuessF20  = {"E430": [0.005, 0.053, 1, 0, 0.00483]};
            skSetInitialGuess(sketch, initialGuessF20);
            skSolve(sketch);
        }
        {
            var Q0;
            Q0=qSketchRegion(id+"F20",true);
            extrude(context, id + "F21", {"entities" : qUnion([Q0]), "operationType" : NewBodyOperationType.REMOVE, "oppositeDirection" : true, "depth" : 0.5 * mm});
        }
        {
            var Q0;
            {var subQ0=sQuery(id+"F2.wireOp",EDGE,"E13");var subQ1=sQuery(id+"F0.wireOp",EDGE,"E3");var subQ2=sQuery(id+"F0.wireOp",EDGE,"E7");Q0=makeQuery(id+"F3.boolean.opBoolean","SPLIT",EDGE,{"disambiguationData":[TD([makeQuery(id+"F1.opExtrude","CAP_FACE",FACE,{"disambiguationData":[OSD([sQuery(id+"F0.wireOp",EDGE,"E0"),sQuery(id+"F0.wireOp",EDGE,"E1"),sQuery(id+"F0.wireOp",EDGE,"E2"),subQ1,sQuery(id+"F0.wireOp",EDGE,"E4"),sQuery(id+"F0.wireOp",EDGE,"E5"),sQuery(id+"F0.wireOp",EDGE,"E6"),subQ2,sQuery(id+"F0.wireOp",EDGE,"E8"),sQuery(id+"F0.wireOp",EDGE,"E9"),sQuery(id+"F0.wireOp",EDGE,"E11"),sQuery(id+"F0.wireOp",EDGE,"E12")])],"isStart":false}),makeQuery(id+"F1.opExtrude","SWEPT_FACE",FACE,{"disambiguationData":[OSD([subQ1])]}),makeQuery(id+"F1.opExtrude","SWEPT_FACE",FACE,{"disambiguationData":[OSD([subQ2])]}),makeQuery(id+"F3.opExtrude","SWEPT_FACE",FACE,{"disambiguationData":[OSD([subQ0])]}),makeQuery(id+"F3.opExtrude","CAP_FACE",FACE,{"disambiguationData":[OSD([subQ0])],"isStart":true})])],"derivedFrom":makeQuery(id+"F1.opExtrude","SWEPT_EDGE",EDGE,{"disambiguationData":[OSD([subQ1,subQ2])]})});}
            cPlane(context, id + "F22", {"entities" : qUnion([Q0]), "cplaneType" : CPlaneType.LINE_ANGLE, "offset" : 25 * mm, "angle" : 255 * degree, "width" : 150 * mm, "height" : 150 * mm});
        }
        {
            var Q0;
            Q0=qCreatedBy(id+"F22.planeOp",FACE);
            var sketch = newSketch(context, id + "F23", { "sketchPlane" : qUnion([Q0])});
            skText(sketch, "E431", { "text": "FLV - v0.6", "fontName": "OpenSans-Bold.ttf"});
            const initialGuessF23  = {"E431": [0.007, -0.01852, 1, 0, 0.0087]};
            skSetInitialGuess(sketch, initialGuessF23);
            skSolve(sketch);
        }
        {
            var Q0;
            Q0=qSketchRegion(id+"F23",true);
            extrude(context, id + "F24", {"entities" : qUnion([Q0]), "operationType" : NewBodyOperationType.REMOVE, "oppositeDirection" : true, "depth" : 1.3 * mm});
        }
        {
            var Q0;
            Q0=makeQuery(id+"F12.boolean.opBoolean","COPY",FACE,{"derivedFrom":makeQuery(id+"F12.opExtrude","SWEPT_FACE",FACE,{"disambiguationData":[OSD([sQuery(id+"F11.wireOp",EDGE,"E20.right")])]})});
            cPlane(context, id + "F25", {"entities" : qUnion([Q0]), "cplaneType" : CPlaneType.OFFSET, "offset" : 0 * mm, "width" : 150 * mm, "height" : 150 * mm});
        }
        {
            var Q0;
            Q0=qCreatedBy(id+"F25.planeOp",FACE);
            var sketch = newSketch(context, id + "F26", { "sketchPlane" : qUnion([Q0])});
            skCircle(sketch, "E432", {"center": v(-11.91, 52.48) * mm, "radius": 0.4 * mm});
            skCircle(sketch, "E433", {"center": v(-13.19, 52.75) * mm, "radius": 0.37 * mm});
            skCircle(sketch, "E434", {"center": v(-12.69, 53.9) * mm, "radius": 0.32 * mm});
            skCircle(sketch, "E435", {"center": v(-11.49, 53.57) * mm, "radius": 0.3 * mm});
            skSolve(sketch);
        }
        {
            var Q0;
            Q0=qSketchRegion(id+"F26",true);
            extrude(context, id + "F27", {"entities" : qUnion([Q0]), "operationType" : NewBodyOperationType.ADD, "depth" : 0.5 * mm, "offsetDistance" : 25 * mm});
        }
        {
            var Q0;
            Q0=makeQuery(id+"F27.opExtrude","CAP_EDGE",EDGE,{"disambiguationData":[OSD([sQuery(id+"F26.wireOp",EDGE,"E435")])],"isStart":false});
            var Q1;
            Q1=makeQuery(id+"F27.opExtrude","CAP_EDGE",EDGE,{"disambiguationData":[OSD([sQuery(id+"F26.wireOp",EDGE,"E432")])],"isStart":false});
            var Q2;
            Q2=makeQuery(id+"F27.opExtrude","CAP_EDGE",EDGE,{"disambiguationData":[OSD([sQuery(id+"F26.wireOp",EDGE,"E433")])],"isStart":false});
            var Q3;
            Q3=makeQuery(id+"F27.opExtrude","CAP_EDGE",EDGE,{"disambiguationData":[OSD([sQuery(id+"F26.wireOp",EDGE,"E434")])],"isStart":false});
            fillet(context, id + "F28", {"entities" : qUnion([Q0, Q1, Q2, Q3]), "radius" : 0.25 * mm, "tangentPropagation" : true, "allowEdgeOverflow" : false});
        }
    });
